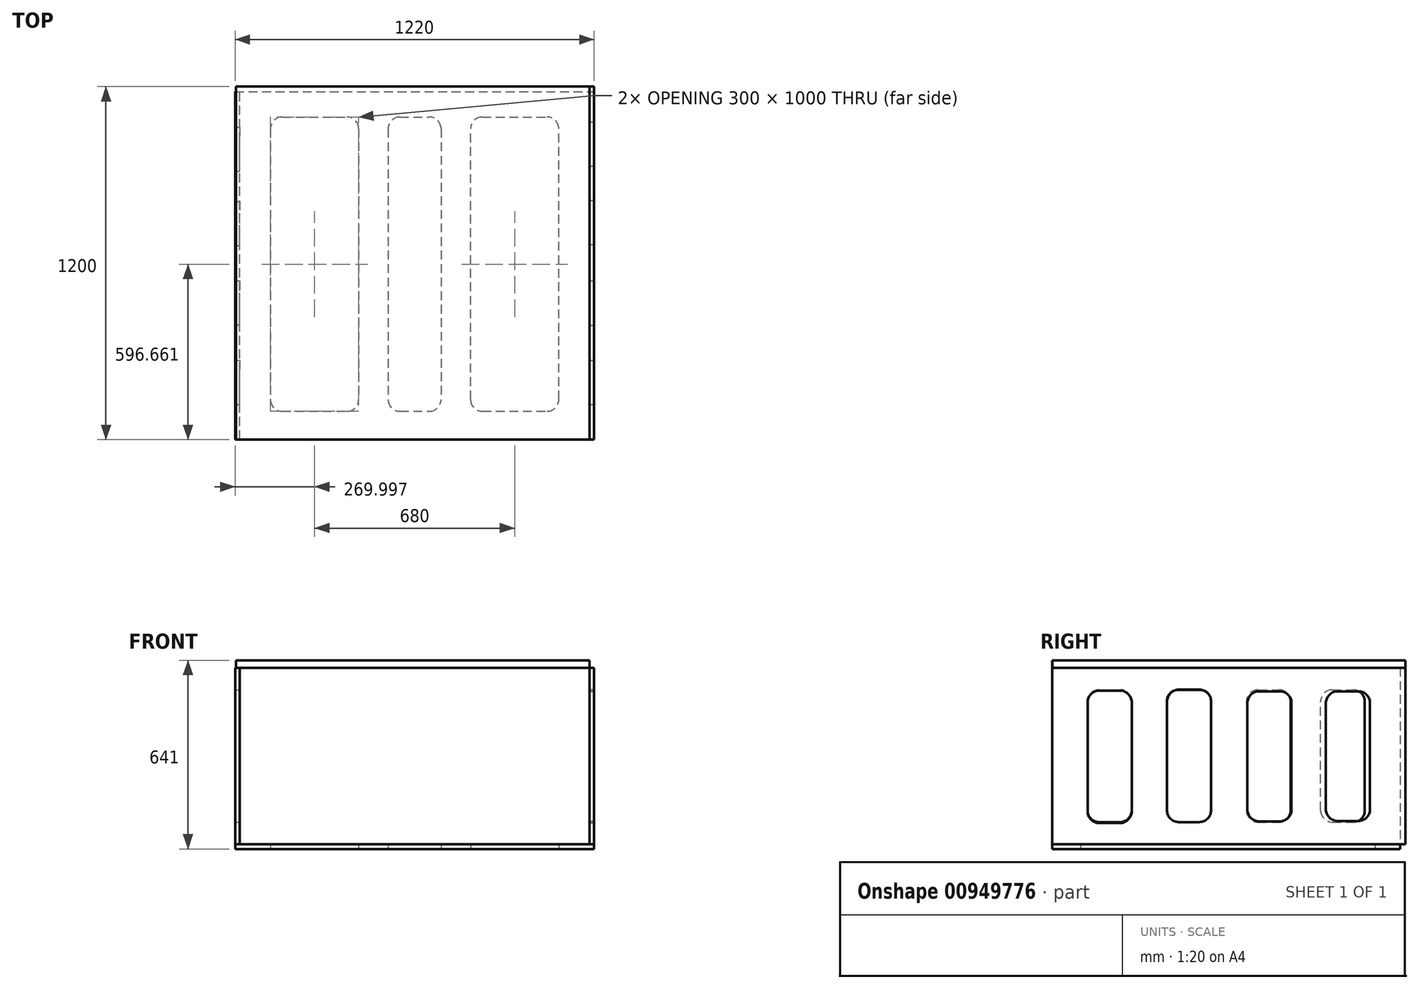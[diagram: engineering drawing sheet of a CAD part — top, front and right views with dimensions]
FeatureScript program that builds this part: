
annotation { "Feature Type Name" : "Feature", "Feature Type Description" : "" }
export const myFeature = defineFeature(function(context is Context, id is Id, definition is map)
    precondition{}
    {
        {
            var Q0;
            Q0=qCreatedBy(makeId("Top.planeOp"),FACE);
            var sketch = newSketch(context, id + "F0", { "sketchPlane" : qUnion([Q0])});
            skLineSegment(sketch, "E0.bottom", {"start": v(-563.9, -494.04) * mm, "end": v(656.1, -494.04) * mm});
            skLineSegment(sketch, "E0.top", {"start": v(-563.9, 705.96) * mm, "end": v(656.1, 705.96) * mm});
            skLineSegment(sketch, "E0.left", {"start": v(-563.9, -494.04) * mm, "end": v(-563.9, 705.96) * mm});
            skLineSegment(sketch, "E0.right", {"start": v(656.1, -494.04) * mm, "end": v(656.1, 705.96) * mm});
            skSolve(sketch);
        }
        {
            var Q0;
            Q0=makeQuery(id+"F0.imprint","IMPRINT",FACE,{"disambiguationData":[TD([[makeQuery(id+"F0.imprint","IMPRINT",EDGE,{"derivedFrom":sQuery(id+"F0.wireOp",EDGE,"E0.bottom")}),1.0]])]});
            var sketch = newSketch(context, id + "F1", { "sketchPlane" : qUnion([Q0])});
            skLineSegment(sketch, "E1.bottom", {"start": v(-403.9, 605.96) * mm, "end": v(-183.9, 605.96) * mm});
            skLineSegment(sketch, "E1.top", {"start": v(-403.9, -394.04) * mm, "end": v(-183.9, -394.04) * mm});
            skLineSegment(sketch, "E1.left", {"start": v(-443.9, 565.96) * mm, "end": v(-443.9, -354.04) * mm});
            skLineSegment(sketch, "E1.right", {"start": v(-143.9, 565.96) * mm, "end": v(-143.9, -354.04) * mm});
            skLineSegment(sketch, "E2.bottom", {"start": v(-3.9, 605.96) * mm, "end": v(96.1, 605.96) * mm});
            skLineSegment(sketch, "E2.top", {"start": v(-3.9, -394.04) * mm, "end": v(96.1, -394.04) * mm});
            skLineSegment(sketch, "E2.left", {"start": v(-43.9, 565.96) * mm, "end": v(-43.9, -354.04) * mm});
            skLineSegment(sketch, "E2.right", {"start": v(136.1, 565.96) * mm, "end": v(136.1, -354.04) * mm});
            skLineSegment(sketch, "E3.bottom", {"start": v(276.1, -394.04) * mm, "end": v(496.1, -394.04) * mm});
            skLineSegment(sketch, "E3.top", {"start": v(276.1, 605.96) * mm, "end": v(496.1, 605.96) * mm});
            skLineSegment(sketch, "E3.left", {"start": v(236.1, -354.04) * mm, "end": v(236.1, 565.96) * mm});
            skLineSegment(sketch, "E3.right", {"start": v(536.1, -354.04) * mm, "end": v(536.1, 565.96) * mm});
            skPoint(sketch, "E4.visualSharp", {"position": v(-443.9, 605.96) * mm});
            skArc(sketch, "E4.filletArc", {"start": v(-403.9, 605.96) * mm, "mid": v(-432.18, 594.25) * mm, "end": v(-443.9, 565.96) * mm});
            skPoint(sketch, "E5.visualSharp", {"position": v(-143.9, 605.96) * mm});
            skArc(sketch, "E5.filletArc", {"start": v(-143.9, 565.96) * mm, "mid": v(-155.6, 594.25) * mm, "end": v(-183.9, 605.96) * mm});
            skPoint(sketch, "E6.visualSharp", {"position": v(-443.9, -394.04) * mm});
            skArc(sketch, "E6.filletArc", {"start": v(-443.9, -354.04) * mm, "mid": v(-432.18, -382.32) * mm, "end": v(-403.9, -394.04) * mm});
            skPoint(sketch, "E7.visualSharp", {"position": v(-143.9, -394.04) * mm});
            skArc(sketch, "E7.filletArc", {"start": v(-183.9, -394.04) * mm, "mid": v(-155.6, -382.32) * mm, "end": v(-143.9, -354.04) * mm});
            skPoint(sketch, "E8.visualSharp", {"position": v(-43.9, -394.04) * mm});
            skArc(sketch, "E8.filletArc", {"start": v(-43.9, -354.04) * mm, "mid": v(-32.18, -382.32) * mm, "end": v(-3.9, -394.04) * mm});
            skPoint(sketch, "E9.visualSharp", {"position": v(136.1, -394.04) * mm});
            skArc(sketch, "E9.filletArc", {"start": v(96.1, -394.04) * mm, "mid": v(124.4, -382.32) * mm, "end": v(136.1, -354.04) * mm});
            skPoint(sketch, "E10.visualSharp", {"position": v(-43.9, 605.96) * mm});
            skArc(sketch, "E10.filletArc", {"start": v(-3.9, 605.96) * mm, "mid": v(-32.18, 594.25) * mm, "end": v(-43.9, 565.96) * mm});
            skPoint(sketch, "E11.visualSharp", {"position": v(136.1, 605.96) * mm});
            skArc(sketch, "E11.filletArc", {"start": v(136.1, 565.96) * mm, "mid": v(124.4, 594.25) * mm, "end": v(96.1, 605.96) * mm});
            skPoint(sketch, "E12.visualSharp", {"position": v(236.1, 605.96) * mm});
            skArc(sketch, "E12.filletArc", {"start": v(276.1, 605.96) * mm, "mid": v(247.82, 594.25) * mm, "end": v(236.1, 565.96) * mm});
            skPoint(sketch, "E13.visualSharp", {"position": v(536.1, 605.96) * mm});
            skArc(sketch, "E13.filletArc", {"start": v(536.1, 565.96) * mm, "mid": v(524.4, 594.25) * mm, "end": v(496.1, 605.96) * mm});
            skPoint(sketch, "E14.visualSharp", {"position": v(536.1, -394.04) * mm});
            skArc(sketch, "E14.filletArc", {"start": v(496.1, -394.04) * mm, "mid": v(524.4, -382.32) * mm, "end": v(536.1, -354.04) * mm});
            skPoint(sketch, "E15.visualSharp", {"position": v(236.1, -394.04) * mm});
            skArc(sketch, "E15.filletArc", {"start": v(236.1, -354.04) * mm, "mid": v(247.82, -382.32) * mm, "end": v(276.1, -394.04) * mm});
            skLineSegment(sketch, "E16.bottom", {"start": v(-563.9, -490.7) * mm, "end": v(656.1, -490.7) * mm});
            skLineSegment(sketch, "E16.top", {"start": v(-563.9, 691.52) * mm, "end": v(656.1, 691.52) * mm});
            skLineSegment(sketch, "E16.left", {"start": v(-563.9, -490.7) * mm, "end": v(-563.9, 691.52) * mm});
            skLineSegment(sketch, "E16.right", {"start": v(656.1, -490.7) * mm, "end": v(656.1, 691.52) * mm});
            skSolve(sketch);
        }
        {
            var Q0;
            Q0=makeQuery(id+"F1.imprint","IMPRINT",FACE,{"disambiguationData":[TD([[makeQuery(id+"F1.imprint","IMPRINT",EDGE,{"derivedFrom":sQuery(id+"F1.wireOp",EDGE,"E1.bottom")}),1.0]])]});
            var sketch = newSketch(context, id + "F2", { "sketchPlane" : qUnion([Q0])});
            skSolve(sketch);
        }
        {
            var Q0;
            Q0=makeQuery(id+"F2.imprint","IMPRINT",FACE,{"disambiguationData":[TD([[makeQuery(id+"F2.imprint","IMPRINT",EDGE,{"derivedFrom":makeQuery(id+"F1.imprint","IMPRINT",EDGE,{"derivedFrom":sQuery(id+"F1.wireOp",EDGE,"E1.bottom")})}),1.0]])]});
            extrude(context, id + "F3", {"entities" : qUnion([Q0]), "depth" : 16 * mm, "offsetDistance" : 25 * mm});
        }
        {
            var Q0;
            Q0=makeQuery(id+"F3.opExtrude","CAP_FACE",FACE,{"disambiguationData":[OSD([sQuery(id+"F1.wireOp",EDGE,"E1.bottom"),sQuery(id+"F1.wireOp",EDGE,"E1.top"),sQuery(id+"F1.wireOp",EDGE,"E1.left"),sQuery(id+"F1.wireOp",EDGE,"E1.right"),sQuery(id+"F1.wireOp",EDGE,"E2.bottom"),sQuery(id+"F1.wireOp",EDGE,"E2.top"),sQuery(id+"F1.wireOp",EDGE,"E2.left"),sQuery(id+"F1.wireOp",EDGE,"E2.right"),sQuery(id+"F1.wireOp",EDGE,"E3.bottom"),sQuery(id+"F1.wireOp",EDGE,"E3.top"),sQuery(id+"F1.wireOp",EDGE,"E3.left"),sQuery(id+"F1.wireOp",EDGE,"E3.right"),sQuery(id+"F1.wireOp",EDGE,"E4.filletArc"),sQuery(id+"F1.wireOp",EDGE,"E5.filletArc"),sQuery(id+"F1.wireOp",EDGE,"E6.filletArc"),sQuery(id+"F1.wireOp",EDGE,"E7.filletArc"),sQuery(id+"F1.wireOp",EDGE,"E8.filletArc"),sQuery(id+"F1.wireOp",EDGE,"E9.filletArc"),sQuery(id+"F1.wireOp",EDGE,"E10.filletArc"),sQuery(id+"F1.wireOp",EDGE,"E11.filletArc"),sQuery(id+"F1.wireOp",EDGE,"E12.filletArc"),sQuery(id+"F1.wireOp",EDGE,"E13.filletArc"),sQuery(id+"F1.wireOp",EDGE,"E14.filletArc"),sQuery(id+"F1.wireOp",EDGE,"E15.filletArc"),sQuery(id+"F1.wireOp",EDGE,"E16.bottom"),sQuery(id+"F1.wireOp",EDGE,"E16.top"),sQuery(id+"F1.wireOp",EDGE,"E16.left"),sQuery(id+"F1.wireOp",EDGE,"E16.right")])],"isStart":false});
            var sketch = newSketch(context, id + "F4", { "sketchPlane" : qUnion([Q0])});
            skLineSegment(sketch, "E17.bottom", {"start": v(-547.9, -490.7) * mm, "end": v(-563.9, -490.7) * mm});
            skLineSegment(sketch, "E17.top", {"start": v(-547.9, 691.52) * mm, "end": v(-563.9, 691.52) * mm});
            skLineSegment(sketch, "E17.left", {"start": v(-563.9, -490.7) * mm, "end": v(-563.9, 691.52) * mm});
            skLineSegment(sketch, "E17.right", {"start": v(-547.9, -490.7) * mm, "end": v(-547.9, 691.52) * mm});
            skSolve(sketch);
        }
        {
            var Q0;
            Q0=makeQuery(id+"F4.imprint","IMPRINT",FACE,{"disambiguationData":[TD([[makeQuery(id+"F4.imprint","IMPRINT",EDGE,{"derivedFrom":sQuery(id+"F4.wireOp",EDGE,"E17.bottom")}),1.0]])]});
            extrude(context, id + "F5", {"entities" : qUnion([Q0]), "depth" : 600 * mm, "offsetDistance" : 25 * mm});
        }
        {
            var Q0;
            Q0=makeQuery(id+"F5.opExtrude","SWEPT_FACE",FACE,{"disambiguationData":[OSD([sQuery(id+"F4.wireOp",EDGE,"E17.right")])]});
            var sketch = newSketch(context, id + "F6", { "sketchPlane" : qUnion([Q0])});
            skLineSegment(sketch, "E18.bottom", {"start": v(-330.7, 541) * mm, "end": v(-260.7, 541) * mm});
            skLineSegment(sketch, "E18.top", {"start": v(-330.7, 91) * mm, "end": v(-260.7, 91) * mm});
            skLineSegment(sketch, "E18.left", {"start": v(-370.7, 501) * mm, "end": v(-370.7, 131) * mm});
            skLineSegment(sketch, "E18.right", {"start": v(-220.7, 501) * mm, "end": v(-220.7, 131) * mm});
            skLineSegment(sketch, "E19.bottom", {"start": v(-60.7, 91) * mm, "end": v(9.3, 91) * mm});
            skLineSegment(sketch, "E19.top", {"start": v(-60.7, 541) * mm, "end": v(9.3, 541) * mm});
            skLineSegment(sketch, "E19.left", {"start": v(-100.7, 131) * mm, "end": v(-100.7, 501) * mm});
            skLineSegment(sketch, "E19.right", {"start": v(49.3, 131) * mm, "end": v(49.3, 501) * mm});
            skLineSegment(sketch, "E20.bottom", {"start": v(209.3, 541) * mm, "end": v(279.3, 541) * mm});
            skLineSegment(sketch, "E20.top", {"start": v(209.3, 91) * mm, "end": v(279.3, 91) * mm});
            skLineSegment(sketch, "E20.left", {"start": v(169.3, 501) * mm, "end": v(169.3, 131) * mm});
            skLineSegment(sketch, "E20.right", {"start": v(319.3, 501) * mm, "end": v(319.3, 131) * mm});
            skLineSegment(sketch, "E21.bottom", {"start": v(461.52, 91) * mm, "end": v(531.52, 91) * mm});
            skLineSegment(sketch, "E21.top", {"start": v(461.52, 541) * mm, "end": v(531.52, 541) * mm});
            skLineSegment(sketch, "E21.left", {"start": v(421.52, 131) * mm, "end": v(421.52, 501) * mm});
            skLineSegment(sketch, "E21.right", {"start": v(571.52, 131) * mm, "end": v(571.52, 501) * mm});
            skPoint(sketch, "E22.visualSharp", {"position": v(-370.7, 541) * mm});
            skArc(sketch, "E22.filletArc", {"start": v(-330.7, 541) * mm, "mid": v(-358.99, 529.28) * mm, "end": v(-370.7, 501) * mm});
            skPoint(sketch, "E23.visualSharp", {"position": v(-220.7, 541) * mm});
            skArc(sketch, "E23.filletArc", {"start": v(-220.7, 501) * mm, "mid": v(-232.42, 529.28) * mm, "end": v(-260.7, 541) * mm});
            skPoint(sketch, "E24.visualSharp", {"position": v(-370.7, 91) * mm});
            skArc(sketch, "E24.filletArc", {"start": v(-370.7, 131) * mm, "mid": v(-358.99, 102.72) * mm, "end": v(-330.7, 91) * mm});
            skPoint(sketch, "E25.visualSharp", {"position": v(-220.7, 91) * mm});
            skArc(sketch, "E25.filletArc", {"start": v(-260.7, 91) * mm, "mid": v(-232.42, 102.72) * mm, "end": v(-220.7, 131) * mm});
            skPoint(sketch, "E26.visualSharp", {"position": v(-100.7, 91) * mm});
            skArc(sketch, "E26.filletArc", {"start": v(-100.7, 131) * mm, "mid": v(-88.99, 102.72) * mm, "end": v(-60.7, 91) * mm});
            skPoint(sketch, "E27.visualSharp", {"position": v(-100.7, 541) * mm});
            skArc(sketch, "E27.filletArc", {"start": v(-60.7, 541) * mm, "mid": v(-88.99, 529.28) * mm, "end": v(-100.7, 501) * mm});
            skPoint(sketch, "E28.visualSharp", {"position": v(49.3, 541) * mm});
            skArc(sketch, "E28.filletArc", {"start": v(49.3, 501) * mm, "mid": v(37.58, 529.28) * mm, "end": v(9.3, 541) * mm});
            skPoint(sketch, "E29.visualSharp", {"position": v(49.3, 91) * mm});
            skArc(sketch, "E29.filletArc", {"start": v(9.3, 91) * mm, "mid": v(37.58, 102.72) * mm, "end": v(49.3, 131) * mm});
            skPoint(sketch, "E30.visualSharp", {"position": v(169.3, 91) * mm});
            skArc(sketch, "E30.filletArc", {"start": v(169.3, 131) * mm, "mid": v(181.01, 102.72) * mm, "end": v(209.3, 91) * mm});
            skPoint(sketch, "E31.visualSharp", {"position": v(169.3, 541) * mm});
            skArc(sketch, "E31.filletArc", {"start": v(209.3, 541) * mm, "mid": v(181.01, 529.28) * mm, "end": v(169.3, 501) * mm});
            skPoint(sketch, "E32.visualSharp", {"position": v(319.3, 541) * mm});
            skArc(sketch, "E32.filletArc", {"start": v(319.3, 501) * mm, "mid": v(307.58, 529.28) * mm, "end": v(279.3, 541) * mm});
            skPoint(sketch, "E33.visualSharp", {"position": v(319.3, 91) * mm});
            skArc(sketch, "E33.filletArc", {"start": v(279.3, 91) * mm, "mid": v(307.58, 102.72) * mm, "end": v(319.3, 131) * mm});
            skPoint(sketch, "E34.visualSharp", {"position": v(421.52, 91) * mm});
            skArc(sketch, "E34.filletArc", {"start": v(421.52, 131) * mm, "mid": v(433.23, 102.72) * mm, "end": v(461.52, 91) * mm});
            skPoint(sketch, "E35.visualSharp", {"position": v(421.52, 541) * mm});
            skArc(sketch, "E35.filletArc", {"start": v(461.52, 541) * mm, "mid": v(433.23, 529.28) * mm, "end": v(421.52, 501) * mm});
            skPoint(sketch, "E36.visualSharp", {"position": v(571.52, 541) * mm});
            skArc(sketch, "E36.filletArc", {"start": v(571.52, 501) * mm, "mid": v(559.8, 529.28) * mm, "end": v(531.52, 541) * mm});
            skPoint(sketch, "E37.visualSharp", {"position": v(571.52, 91) * mm});
            skArc(sketch, "E37.filletArc", {"start": v(531.52, 91) * mm, "mid": v(559.8, 102.72) * mm, "end": v(571.52, 131) * mm});
            skSolve(sketch);
        }
        {
            var Q0;
            Q0=makeQuery(id+"F6.imprint","IMPRINT",FACE,{"disambiguationData":[TD([[makeQuery(id+"F6.imprint","IMPRINT",EDGE,{"derivedFrom":sQuery(id+"F6.wireOp",EDGE,"E19.bottom")}),1.0]])]});
            var Q1;
            Q1=makeQuery(id+"F6.imprint","IMPRINT",FACE,{"disambiguationData":[TD([[makeQuery(id+"F6.imprint","IMPRINT",EDGE,{"derivedFrom":sQuery(id+"F6.wireOp",EDGE,"E21.bottom")}),1.0]])]});
            var Q2;
            Q2=makeQuery(id+"F6.imprint","IMPRINT",FACE,{"disambiguationData":[TD([[makeQuery(id+"F6.imprint","IMPRINT",EDGE,{"derivedFrom":sQuery(id+"F6.wireOp",EDGE,"E20.bottom")}),-1.0]])]});
            var Q3;
            Q3=makeQuery(id+"F6.imprint","IMPRINT",FACE,{"disambiguationData":[TD([[makeQuery(id+"F6.imprint","IMPRINT",EDGE,{"derivedFrom":sQuery(id+"F6.wireOp",EDGE,"E18.bottom")}),-1.0]])]});
            extrude(context, id + "F7", {"entities" : qUnion([Q0, Q1, Q2, Q3]), "operationType" : NewBodyOperationType.REMOVE, "oppositeDirection" : true, "depth" : 16 * mm, "offsetDistance" : 25 * mm});
        }
        {
            var Q0;
            Q0=makeQuery(id+"F3.opExtrude","CAP_FACE",FACE,{"disambiguationData":[OSD([sQuery(id+"F1.wireOp",EDGE,"E1.bottom"),sQuery(id+"F1.wireOp",EDGE,"E1.top"),sQuery(id+"F1.wireOp",EDGE,"E1.left"),sQuery(id+"F1.wireOp",EDGE,"E1.right"),sQuery(id+"F1.wireOp",EDGE,"E2.bottom"),sQuery(id+"F1.wireOp",EDGE,"E2.top"),sQuery(id+"F1.wireOp",EDGE,"E2.left"),sQuery(id+"F1.wireOp",EDGE,"E2.right"),sQuery(id+"F1.wireOp",EDGE,"E3.bottom"),sQuery(id+"F1.wireOp",EDGE,"E3.top"),sQuery(id+"F1.wireOp",EDGE,"E3.left"),sQuery(id+"F1.wireOp",EDGE,"E3.right"),sQuery(id+"F1.wireOp",EDGE,"E4.filletArc"),sQuery(id+"F1.wireOp",EDGE,"E5.filletArc"),sQuery(id+"F1.wireOp",EDGE,"E6.filletArc"),sQuery(id+"F1.wireOp",EDGE,"E7.filletArc"),sQuery(id+"F1.wireOp",EDGE,"E8.filletArc"),sQuery(id+"F1.wireOp",EDGE,"E9.filletArc"),sQuery(id+"F1.wireOp",EDGE,"E10.filletArc"),sQuery(id+"F1.wireOp",EDGE,"E11.filletArc"),sQuery(id+"F1.wireOp",EDGE,"E12.filletArc"),sQuery(id+"F1.wireOp",EDGE,"E13.filletArc"),sQuery(id+"F1.wireOp",EDGE,"E14.filletArc"),sQuery(id+"F1.wireOp",EDGE,"E15.filletArc"),sQuery(id+"F1.wireOp",EDGE,"E16.bottom"),sQuery(id+"F1.wireOp",EDGE,"E16.top"),sQuery(id+"F1.wireOp",EDGE,"E16.left"),sQuery(id+"F1.wireOp",EDGE,"E16.right")])],"isStart":false});
            var sketch = newSketch(context, id + "F8", { "sketchPlane" : qUnion([Q0])});
            skLineSegment(sketch, "E38.bottom", {"start": v(656.1, -490.7) * mm, "end": v(640.1, -490.7) * mm});
            skLineSegment(sketch, "E38.top", {"start": v(656.1, 709.3) * mm, "end": v(640.1, 709.3) * mm});
            skLineSegment(sketch, "E38.left", {"start": v(656.1, -490.7) * mm, "end": v(656.1, 709.3) * mm});
            skLineSegment(sketch, "E38.right", {"start": v(640.1, -490.7) * mm, "end": v(640.1, 709.3) * mm});
            skSolve(sketch);
        }
        {
            var Q0;
            Q0 = qSketchRegion(id + "F8", true);
            var Q1;
            {var subQ0=sQuery(id+"F8.wireOp",EDGE,"E38.bottom");Q1=makeQuery(id+"F8.imprint","IMPRINT",FACE,{"disambiguationData":[TD([[makeQuery(id+"F8.imprint","IMPRINT",EDGE,{"derivedFrom":subQ0}),1.0]])]});}
            extrude(context, id + "F9", {"entities" : qUnion([Q0, Q1]), "depth" : 600 * mm, "offsetDistance" : 25 * mm});
        }
        {
            var Q0;
            Q0=makeQuery(id+"F9.opExtrude","SWEPT_FACE",FACE,{"disambiguationData":[OSD([sQuery(id+"F8.wireOp",EDGE,"E38.left")])]});
            var sketch = newSketch(context, id + "F10", { "sketchPlane" : qUnion([Q0])});
            skLineSegment(sketch, "E39.bottom", {"start": v(-330.7, 88.1) * mm, "end": v(-260.7, 88.1) * mm});
            skLineSegment(sketch, "E39.top", {"start": v(-330.7, 538.2) * mm, "end": v(-260.7, 538.2) * mm});
            skLineSegment(sketch, "E39.left", {"start": v(-370.7, 128.1) * mm, "end": v(-370.7, 498.2) * mm});
            skLineSegment(sketch, "E39.right", {"start": v(-220.7, 128.1) * mm, "end": v(-220.7, 498.2) * mm});
            skLineSegment(sketch, "E40.bottom", {"start": v(-61.05, 91.52) * mm, "end": v(8.95, 91.52) * mm});
            skLineSegment(sketch, "E40.top", {"start": v(-61.05, 541.62) * mm, "end": v(8.95, 541.62) * mm});
            skLineSegment(sketch, "E40.left", {"start": v(-101.05, 131.52) * mm, "end": v(-101.05, 501.62) * mm});
            skLineSegment(sketch, "E40.right", {"start": v(48.95, 131.52) * mm, "end": v(48.95, 501.62) * mm});
            skLineSegment(sketch, "E41.bottom", {"start": v(212.43, 93.8) * mm, "end": v(282.43, 93.8) * mm});
            skLineSegment(sketch, "E41.top", {"start": v(212.43, 535.92) * mm, "end": v(282.43, 535.92) * mm});
            skLineSegment(sketch, "E41.left", {"start": v(172.43, 133.8) * mm, "end": v(172.43, 495.92) * mm});
            skLineSegment(sketch, "E41.right", {"start": v(322.43, 133.8) * mm, "end": v(322.43, 495.92) * mm});
            skLineSegment(sketch, "E42.bottom", {"start": v(479.3, 94.93) * mm, "end": v(549.3, 94.93) * mm});
            skLineSegment(sketch, "E42.top", {"start": v(479.3, 535.92) * mm, "end": v(549.3, 535.92) * mm});
            skLineSegment(sketch, "E42.left", {"start": v(439.3, 134.93) * mm, "end": v(439.3, 495.92) * mm});
            skLineSegment(sketch, "E42.right", {"start": v(589.3, 134.93) * mm, "end": v(589.3, 495.92) * mm});
            skPoint(sketch, "E43.visualSharp", {"position": v(-370.7, 538.2) * mm});
            skArc(sketch, "E43.filletArc", {"start": v(-330.7, 538.2) * mm, "mid": v(-358.99, 526.49) * mm, "end": v(-370.7, 498.2) * mm});
            skPoint(sketch, "E44.visualSharp", {"position": v(-220.7, 538.2) * mm});
            skArc(sketch, "E44.filletArc", {"start": v(-220.7, 498.2) * mm, "mid": v(-232.42, 526.49) * mm, "end": v(-260.7, 538.2) * mm});
            skPoint(sketch, "E45.visualSharp", {"position": v(-220.7, 88.1) * mm});
            skArc(sketch, "E45.filletArc", {"start": v(-260.7, 88.1) * mm, "mid": v(-232.42, 99.81) * mm, "end": v(-220.7, 128.1) * mm});
            skPoint(sketch, "E46.visualSharp", {"position": v(-370.7, 88.1) * mm});
            skArc(sketch, "E46.filletArc", {"start": v(-370.7, 128.1) * mm, "mid": v(-358.99, 99.81) * mm, "end": v(-330.7, 88.1) * mm});
            skPoint(sketch, "E47.visualSharp", {"position": v(-101.05, 91.52) * mm});
            skArc(sketch, "E47.filletArc", {"start": v(-101.05, 131.52) * mm, "mid": v(-89.33, 103.23) * mm, "end": v(-61.05, 91.52) * mm});
            skPoint(sketch, "E48.visualSharp", {"position": v(48.95, 91.52) * mm});
            skArc(sketch, "E48.filletArc", {"start": v(8.95, 91.52) * mm, "mid": v(37.24, 103.23) * mm, "end": v(48.95, 131.52) * mm});
            skPoint(sketch, "E49.visualSharp", {"position": v(48.95, 541.62) * mm});
            skArc(sketch, "E49.filletArc", {"start": v(48.95, 501.62) * mm, "mid": v(37.24, 529.9) * mm, "end": v(8.95, 541.62) * mm});
            skPoint(sketch, "E50.visualSharp", {"position": v(-101.05, 541.62) * mm});
            skArc(sketch, "E50.filletArc", {"start": v(-61.05, 541.62) * mm, "mid": v(-89.33, 529.9) * mm, "end": v(-101.05, 501.62) * mm});
            skPoint(sketch, "E51.visualSharp", {"position": v(172.43, 535.92) * mm});
            skArc(sketch, "E51.filletArc", {"start": v(212.43, 535.92) * mm, "mid": v(184.15, 524.2) * mm, "end": v(172.43, 495.92) * mm});
            skPoint(sketch, "E52.visualSharp", {"position": v(322.43, 535.92) * mm});
            skArc(sketch, "E52.filletArc", {"start": v(322.43, 495.92) * mm, "mid": v(310.72, 524.2) * mm, "end": v(282.43, 535.92) * mm});
            skPoint(sketch, "E53.visualSharp", {"position": v(439.3, 535.92) * mm});
            skArc(sketch, "E53.filletArc", {"start": v(479.3, 535.92) * mm, "mid": v(451.01, 524.2) * mm, "end": v(439.3, 495.92) * mm});
            skPoint(sketch, "E54.visualSharp", {"position": v(589.3, 535.92) * mm});
            skArc(sketch, "E54.filletArc", {"start": v(589.3, 495.92) * mm, "mid": v(577.58, 524.2) * mm, "end": v(549.3, 535.92) * mm});
            skPoint(sketch, "E55.visualSharp", {"position": v(172.43, 93.8) * mm});
            skArc(sketch, "E55.filletArc", {"start": v(172.43, 133.8) * mm, "mid": v(184.15, 105.51) * mm, "end": v(212.43, 93.8) * mm});
            skPoint(sketch, "E56.visualSharp", {"position": v(322.43, 93.8) * mm});
            skArc(sketch, "E56.filletArc", {"start": v(282.43, 93.8) * mm, "mid": v(310.72, 105.51) * mm, "end": v(322.43, 133.8) * mm});
            skPoint(sketch, "E57.visualSharp", {"position": v(439.3, 94.93) * mm});
            skArc(sketch, "E57.filletArc", {"start": v(439.3, 134.93) * mm, "mid": v(451.01, 106.65) * mm, "end": v(479.3, 94.93) * mm});
            skPoint(sketch, "E58.visualSharp", {"position": v(589.3, 94.93) * mm});
            skArc(sketch, "E58.filletArc", {"start": v(549.3, 94.93) * mm, "mid": v(577.58, 106.65) * mm, "end": v(589.3, 134.93) * mm});
            skSolve(sketch);
        }
        {
            var Q0;
            Q0=makeQuery(id+"F10.imprint","IMPRINT",FACE,{"disambiguationData":[TD([[makeQuery(id+"F10.imprint","IMPRINT",EDGE,{"derivedFrom":sQuery(id+"F10.wireOp",EDGE,"E40.bottom")}),1.0]])]});
            var Q1;
            Q1=makeQuery(id+"F10.imprint","IMPRINT",FACE,{"disambiguationData":[TD([[makeQuery(id+"F10.imprint","IMPRINT",EDGE,{"derivedFrom":sQuery(id+"F10.wireOp",EDGE,"E41.bottom")}),1.0]])]});
            var Q2;
            Q2=makeQuery(id+"F10.imprint","IMPRINT",FACE,{"disambiguationData":[TD([[makeQuery(id+"F10.imprint","IMPRINT",EDGE,{"derivedFrom":sQuery(id+"F10.wireOp",EDGE,"E39.bottom")}),1.0]])]});
            var Q3;
            Q3=makeQuery(id+"F10.imprint","IMPRINT",FACE,{"disambiguationData":[TD([[makeQuery(id+"F10.imprint","IMPRINT",EDGE,{"derivedFrom":sQuery(id+"F10.wireOp",EDGE,"E42.bottom")}),1.0]])]});
            extrude(context, id + "F11", {"entities" : qUnion([Q0, Q1, Q2, Q3]), "operationType" : NewBodyOperationType.REMOVE, "oppositeDirection" : true, "depth" : 16 * mm, "offsetDistance" : 25 * mm});
        }
        {
            var Q0;
            Q0=makeQuery(id+"F9.opExtrude","CAP_FACE",FACE,{"disambiguationData":[OSD([sQuery(id+"F8.wireOp",EDGE,"E38.bottom"),sQuery(id+"F8.wireOp",EDGE,"E38.top"),sQuery(id+"F8.wireOp",EDGE,"E38.left"),sQuery(id+"F8.wireOp",EDGE,"E38.right")])],"isStart":false});
            var sketch = newSketch(context, id + "F12", { "sketchPlane" : qUnion([Q0])});
            skLineSegment(sketch, "E59", {"start": v(656.1, -490.7) * mm, "end": v(656.1, 709.3) * mm});
            skLineSegment(sketch, "E60", {"start": v(656.1, 709.3) * mm, "end": v(-561.32, 709.3) * mm});
            skLineSegment(sketch, "E61", {"start": v(-561.32, 709.3) * mm, "end": v(-561.32, -488.88) * mm});
            skLineSegment(sketch, "E62", {"start": v(-561.32, -488.88) * mm, "end": v(640.1, -490.7) * mm});
            skSolve(sketch);
        }
        {
            var Q0;
            {var subQ2=sQuery(id+"F12.wireOp",EDGE,"E61");Q0=makeQuery(id+"F12.imprint","IMPRINT",FACE,{"disambiguationData":[TD([[makeQuery(id+"F12.imprint","IMPRINT",EDGE,{"derivedFrom":subQ2}),1.0]])]});}
            extrude(context, id + "F13", {"entities" : qUnion([Q0]), "operationType" : NewBodyOperationType.ADD, "depth" : 25 * mm, "offsetDistance" : 25 * mm});
        }
    });
